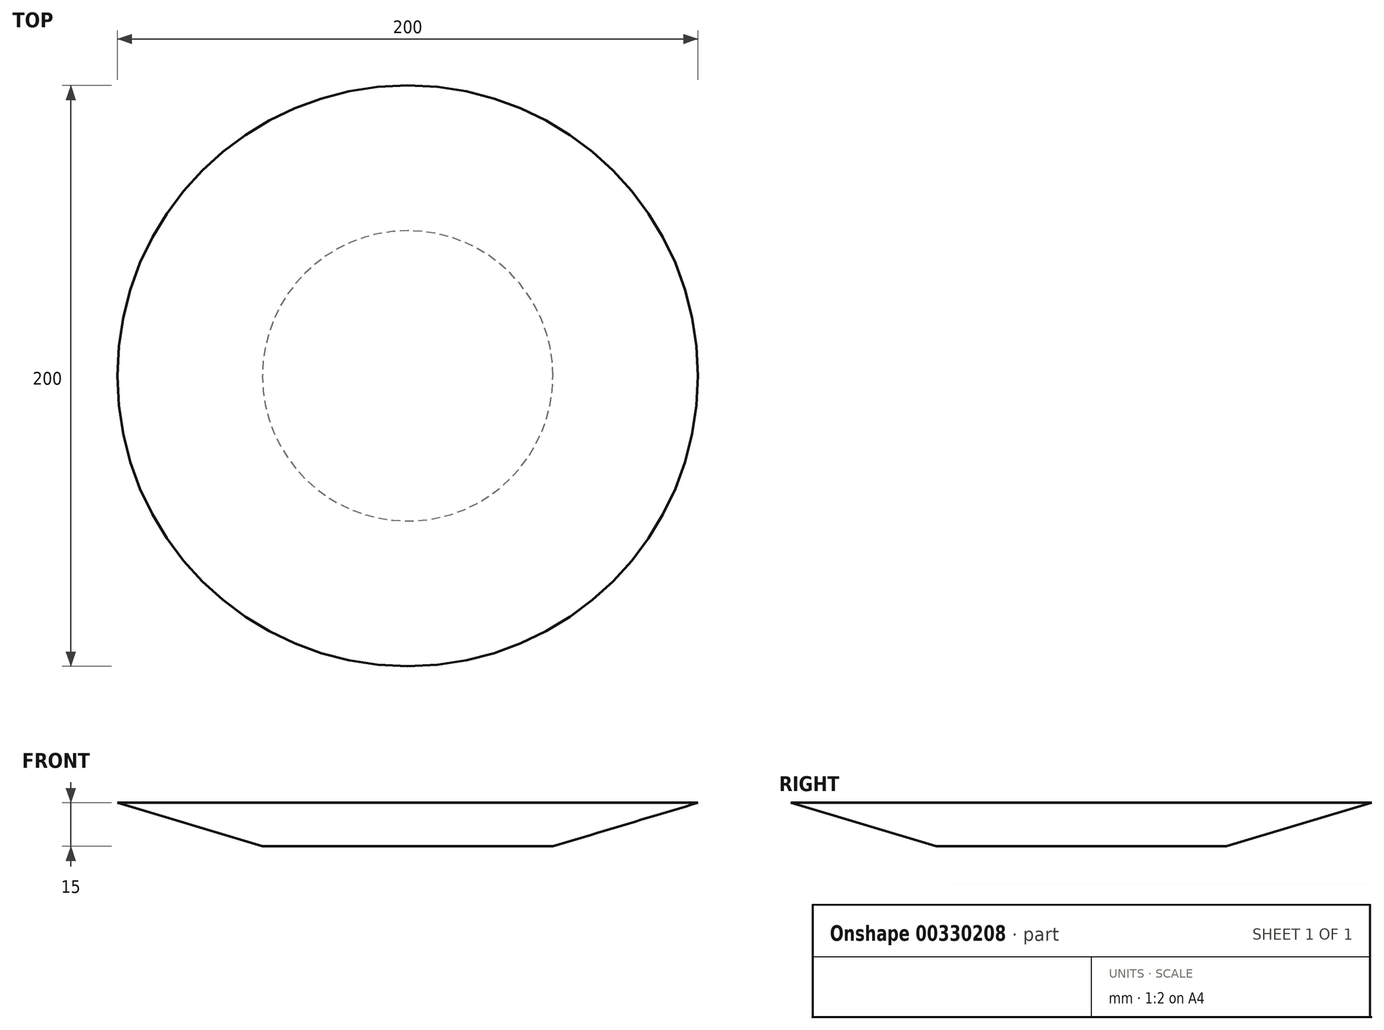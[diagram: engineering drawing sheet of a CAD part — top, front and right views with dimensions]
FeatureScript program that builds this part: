
annotation { "Feature Type Name" : "Feature", "Feature Type Description" : "" }
export const myFeature = defineFeature(function(context is Context, id is Id, definition is map)
    precondition{}
    {
        {
            var Q0;
            Q0=qCreatedBy(makeId("Top.planeOp"),FACE);
            var sketch = newSketch(context, id + "F0", { "sketchPlane" : qUnion([Q0])});
            skCircle(sketch, "E0", {"center": v(0, 0) * mm, "radius": 50 * mm});
            skSolve(sketch);
        }
        {
            var Q0;
            Q0=qCreatedBy(makeId("Top.planeOp"),FACE);
            cPlane(context, id + "F1", {"entities" : qUnion([Q0]), "cplaneType" : CPlaneType.OFFSET, "offset" : 15 * mm, "width" : 150 * mm, "height" : 150 * mm});
        }
        {
            var Q0;
            Q0=qCreatedBy(id+"F1.planeOp",FACE);
            var sketch = newSketch(context, id + "F2", { "sketchPlane" : qUnion([Q0])});
            skCircle(sketch, "E1", {"center": v(0, 0) * mm, "radius": 100 * mm});
            skSolve(sketch);
        }
        {
            var Q0;
            Q0 = qSketchRegion(id + "F2", true);
            var Q1;
            Q1 = qSketchRegion(id + "F0", true);
            loft(context, id + "F3", {"sheetProfilesArray" : [{ "sheetProfileEntities" : qUnion([Q0]) }, { "sheetProfileEntities" : qUnion([Q1]) }]});
        }
    });
